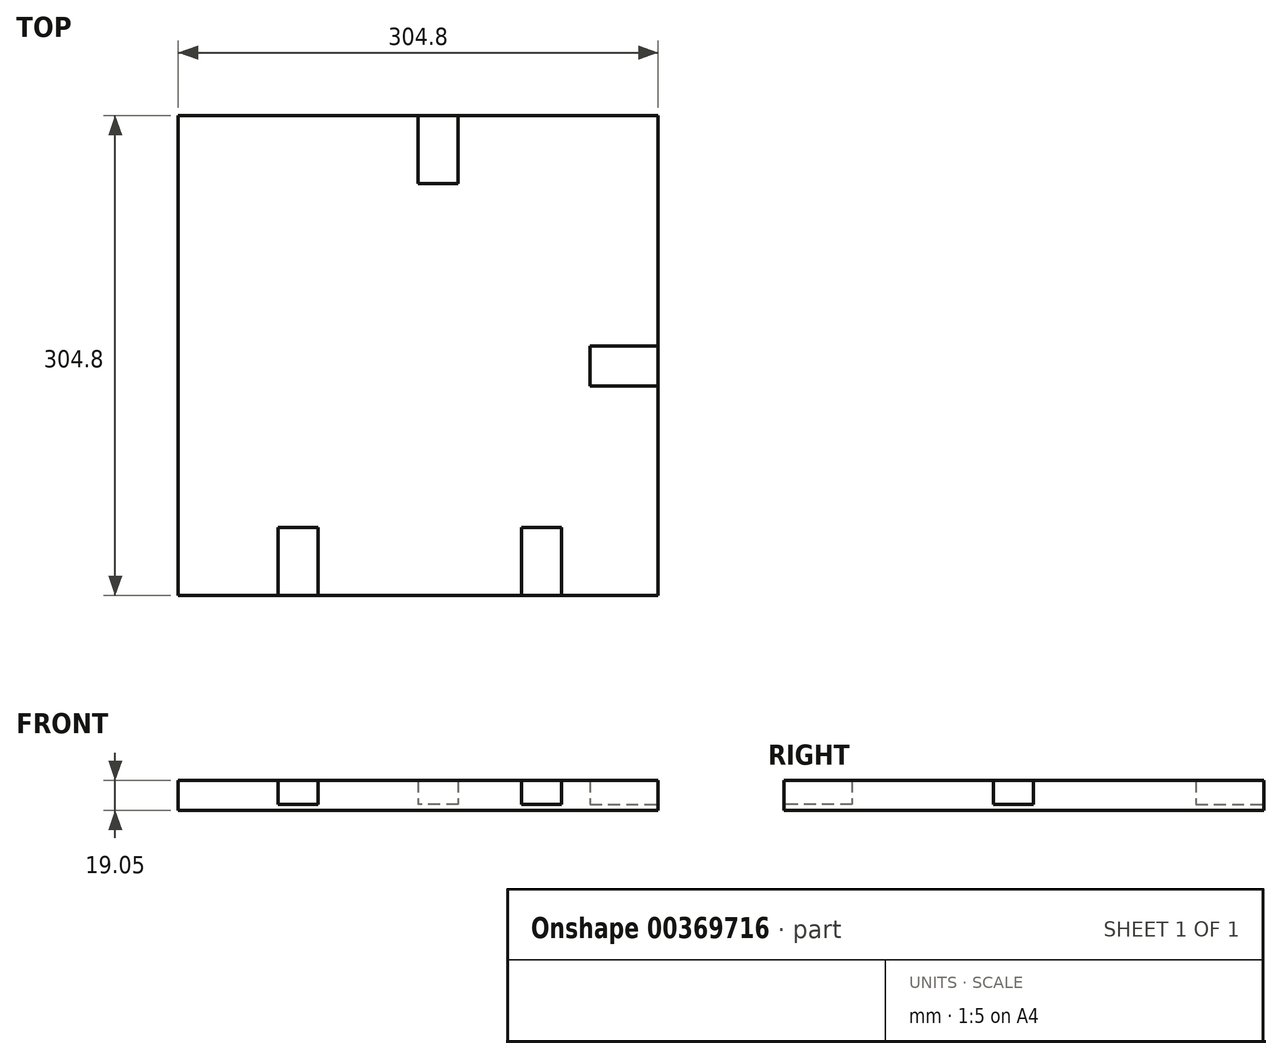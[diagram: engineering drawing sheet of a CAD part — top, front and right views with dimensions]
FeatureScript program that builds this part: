
annotation { "Feature Type Name" : "Feature", "Feature Type Description" : "" }
export const myFeature = defineFeature(function(context is Context, id is Id, definition is map)
    precondition{}
    {
        {
            var Q0;
            Q0=qCreatedBy(makeId("Top.planeOp"),FACE);
            var sketch = newSketch(context, id + "F0", { "sketchPlane" : qUnion([Q0])});
            skLineSegment(sketch, "E0.bottom", {"start": v(0, 0) * mm, "end": v(-304.8, 0) * mm});
            skLineSegment(sketch, "E0.top", {"start": v(0, 304.8) * mm, "end": v(-304.8, 304.8) * mm});
            skLineSegment(sketch, "E0.left", {"start": v(0, 0) * mm, "end": v(0, 304.8) * mm});
            skLineSegment(sketch, "E0.right", {"start": v(-304.8, 0) * mm, "end": v(-304.8, 304.8) * mm});
            skSolve(sketch);
        }
        {
            var Q0;
            Q0 = qSketchRegion(id + "F0", true);
            extrude(context, id + "F1", {"entities" : qUnion([Q0]), "depth" : 19.05 * mm});
        }
        {
            var Q0;
            Q0=makeQuery(id+"F1.opExtrude","SWEPT_FACE",FACE,{"disambiguationData":[OSD([sQuery(id+"F0.wireOp",EDGE,"E0.bottom")])]});
            var sketch = newSketch(context, id + "F2", { "sketchPlane" : qUnion([Q0])});
            skLineSegment(sketch, "E1.bottom", {"start": v(-241.3, 19.05) * mm, "end": v(-215.9, 19.05) * mm});
            skLineSegment(sketch, "E1.top", {"start": v(-241.3, 3.81) * mm, "end": v(-215.9, 3.81) * mm});
            skLineSegment(sketch, "E1.left", {"start": v(-241.3, 19.05) * mm, "end": v(-241.3, 3.81) * mm});
            skLineSegment(sketch, "E1.right", {"start": v(-215.9, 19.05) * mm, "end": v(-215.9, 3.81) * mm});
            skSolve(sketch);
        }
        {
            var Q0;
            Q0 = qSketchRegion(id + "F2", true);
            extrude(context, id + "F3", {"entities" : qUnion([Q0]), "operationType" : NewBodyOperationType.REMOVE, "oppositeDirection" : true, "depth" : 43.18 * mm});
        }
        {
            var Q0;
            Q0=makeQuery(id+"F1.opExtrude","SWEPT_FACE",FACE,{"disambiguationData":[OSD([sQuery(id+"F0.wireOp",EDGE,"E0.bottom")])]});
            var sketch = newSketch(context, id + "F4", { "sketchPlane" : qUnion([Q0])});
            skLineSegment(sketch, "E2.bottom", {"start": v(-86.73, 19.05) * mm, "end": v(-61.33, 19.05) * mm});
            skLineSegment(sketch, "E2.top", {"start": v(-86.73, 3.81) * mm, "end": v(-61.33, 3.81) * mm});
            skLineSegment(sketch, "E2.left", {"start": v(-86.73, 19.05) * mm, "end": v(-86.73, 3.81) * mm});
            skLineSegment(sketch, "E2.right", {"start": v(-61.33, 19.05) * mm, "end": v(-61.33, 3.81) * mm});
            skSolve(sketch);
        }
        {
            var Q0;
            Q0 = qSketchRegion(id + "F4", true);
            extrude(context, id + "F5", {"entities" : qUnion([Q0]), "operationType" : NewBodyOperationType.REMOVE, "oppositeDirection" : true, "depth" : 43.18 * mm});
        }
        {
            var Q0;
            Q0=makeQuery(id+"F1.opExtrude","SWEPT_FACE",FACE,{"disambiguationData":[OSD([sQuery(id+"F0.wireOp",EDGE,"E0.top")])]});
            var sketch = newSketch(context, id + "F6", { "sketchPlane" : qUnion([Q0])});
            skLineSegment(sketch, "E3.bottom", {"start": v(127, 19.05) * mm, "end": v(152.4, 19.05) * mm});
            skLineSegment(sketch, "E3.top", {"start": v(127, 3.81) * mm, "end": v(152.4, 3.81) * mm});
            skLineSegment(sketch, "E3.left", {"start": v(127, 19.05) * mm, "end": v(127, 3.81) * mm});
            skLineSegment(sketch, "E3.right", {"start": v(152.4, 19.05) * mm, "end": v(152.4, 3.81) * mm});
            skSolve(sketch);
        }
        {
            var Q0;
            Q0 = qSketchRegion(id + "F6", true);
            extrude(context, id + "F7", {"entities" : qUnion([Q0]), "operationType" : NewBodyOperationType.REMOVE, "oppositeDirection" : true, "depth" : 43.18 * mm});
        }
        {
            var Q0;
            Q0=makeQuery(id+"F1.opExtrude","SWEPT_FACE",FACE,{"disambiguationData":[OSD([sQuery(id+"F0.wireOp",EDGE,"E0.left")])]});
            var sketch = newSketch(context, id + "F8", { "sketchPlane" : qUnion([Q0])});
            skLineSegment(sketch, "E4.bottom", {"start": v(132.94, 19.05) * mm, "end": v(158.34, 19.05) * mm});
            skLineSegment(sketch, "E4.top", {"start": v(132.94, 3.81) * mm, "end": v(158.34, 3.81) * mm});
            skLineSegment(sketch, "E4.left", {"start": v(132.94, 19.05) * mm, "end": v(132.94, 3.81) * mm});
            skLineSegment(sketch, "E4.right", {"start": v(158.34, 19.05) * mm, "end": v(158.34, 3.81) * mm});
            skSolve(sketch);
        }
        {
            var Q0;
            Q0 = qSketchRegion(id + "F8", true);
            extrude(context, id + "F9", {"entities" : qUnion([Q0]), "operationType" : NewBodyOperationType.REMOVE, "oppositeDirection" : true, "depth" : 43.18 * mm});
        }
    });
